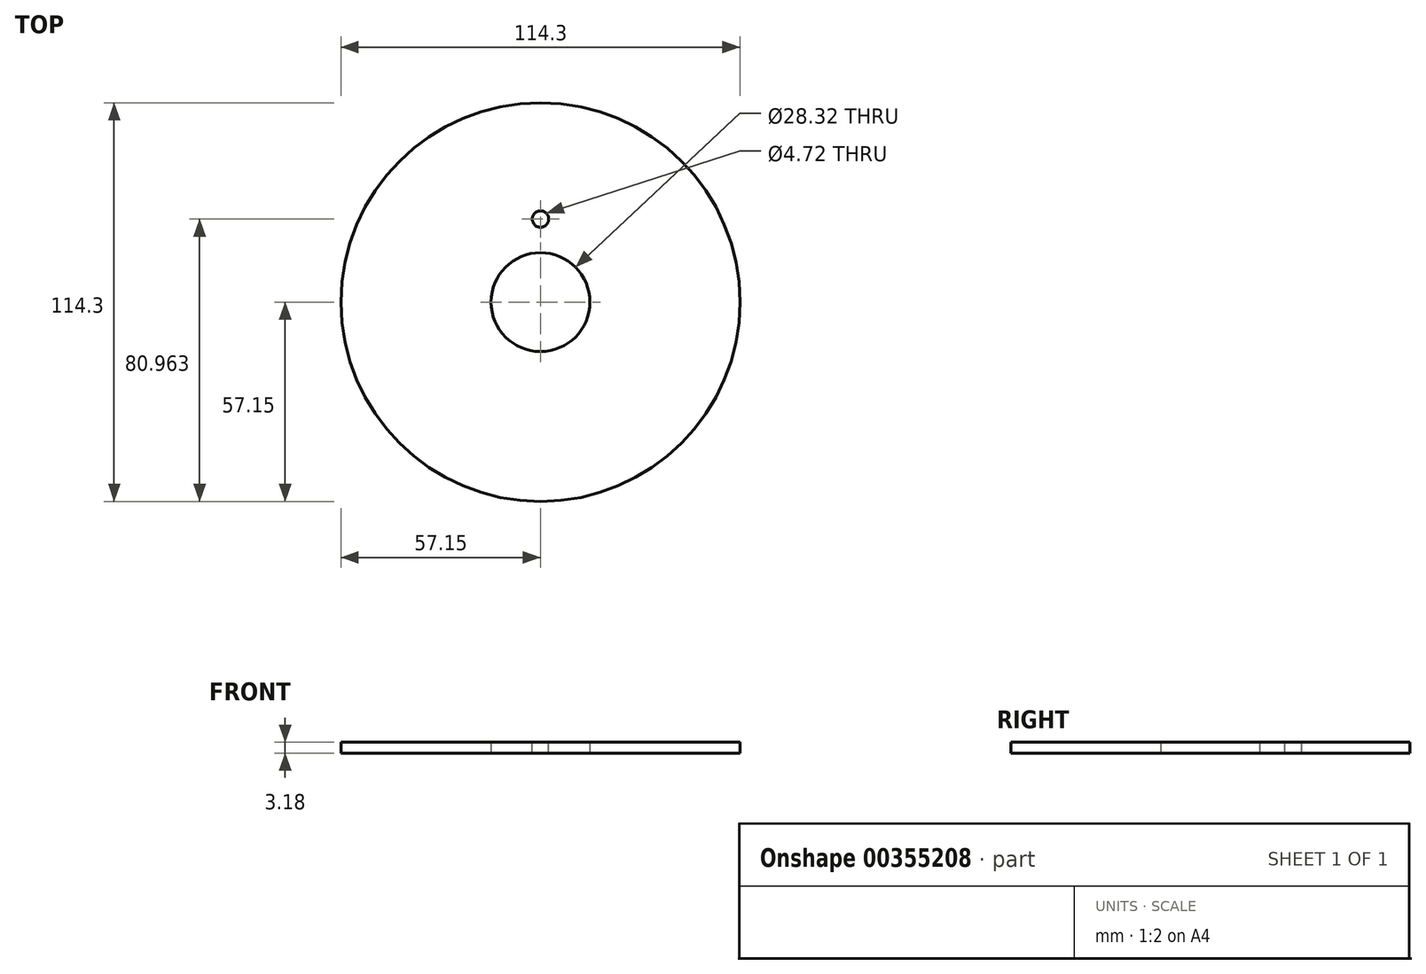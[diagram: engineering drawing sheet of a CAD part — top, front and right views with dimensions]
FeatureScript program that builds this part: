
annotation { "Feature Type Name" : "Feature", "Feature Type Description" : "" }
export const myFeature = defineFeature(function(context is Context, id is Id, definition is map)
    precondition{}
    {
        {
            var Q0;
            Q0=qCreatedBy(makeId("Top.planeOp"),FACE);
            var sketch = newSketch(context, id + "F0", { "sketchPlane" : qUnion([Q0])});
            skCircle(sketch, "E0", {"center": v(0, 0) * mm, "radius": 57.15 * mm});
            skCircle(sketch, "E1", {"center": v(0, 0) * mm, "radius": 14.16 * mm});
            skSolve(sketch);
        }
        {
            var Q0;
            Q0=makeQuery(id+"F0.imprint","IMPRINT",FACE,{"disambiguationData":[TD([[makeQuery(id+"F0.imprint","IMPRINT",EDGE,{"derivedFrom":sQuery(id+"F0.wireOp",EDGE,"E0")}),1.0]])]});
            extrude(context, id + "F1", {"entities" : qUnion([Q0]), "depth" : 3.17 * mm});
        }
        {
            var Q0;
            Q0=makeQuery(id+"F1.opExtrude","CAP_FACE",FACE,{"disambiguationData":[OSD([sQuery(id+"F0.wireOp",EDGE,"E0"),sQuery(id+"F0.wireOp",EDGE,"E1")])],"isStart":false});
            var sketch = newSketch(context, id + "F2", { "sketchPlane" : qUnion([Q0])});
            skCircle(sketch, "E2", {"center": v(0, 23.81) * mm, "radius": 2.36 * mm});
            skCircle(sketch, "E3", {"center": v(0, 76.2) * mm, "radius": 2.36 * mm, "construction": true});
            skCircle(sketch, "E4", {"center": v(25.4, 44) * mm, "radius": 2.36 * mm, "construction": true});
            skLineSegment(sketch, "E5", {"start": v(0, 0) * mm, "end": v(25.4, 44) * mm, "construction": true});
            skSolve(sketch);
        }
        {
            var Q0;
            Q0=qSketchRegion(id+"F2",true);
            extrude(context, id + "F3", {"entities" : qUnion([Q0]), "operationType" : NewBodyOperationType.REMOVE, "endBound" : BoundingType.THROUGH_ALL, "oppositeDirection" : true, "depth" : 25.4 * mm});
        }
    });
